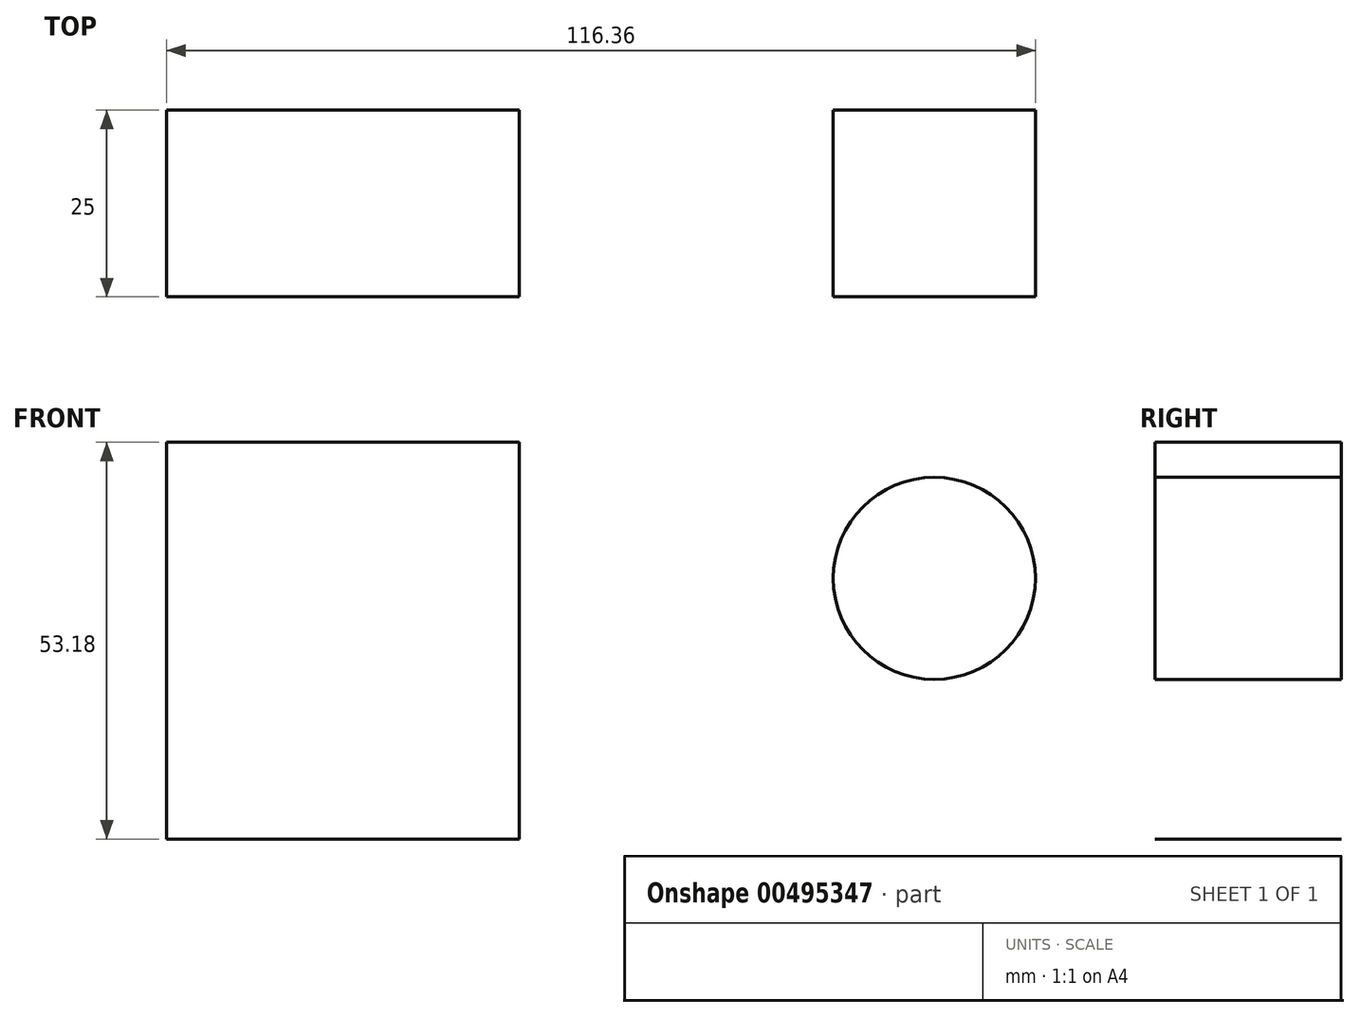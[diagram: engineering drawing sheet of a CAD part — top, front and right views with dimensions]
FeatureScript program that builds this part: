
annotation { "Feature Type Name" : "Feature", "Feature Type Description" : "" }
export const myFeature = defineFeature(function(context is Context, id is Id, definition is map)
    precondition{}
    {
        {
            var Q0;
            Q0=qCreatedBy(makeId("Front.planeOp"),FACE);
            var sketch = newSketch(context, id + "F0", { "sketchPlane" : qUnion([Q0])});
            skLineSegment(sketch, "E0.bottom", {"start": v(-68.86, 20.15) * mm, "end": v(-21.65, 20.15) * mm});
            skLineSegment(sketch, "E0.top", {"start": v(-68.86, -33.03) * mm, "end": v(-21.65, -33.03) * mm});
            skLineSegment(sketch, "E0.left", {"start": v(-68.86, 20.15) * mm, "end": v(-68.86, -33.03) * mm});
            skLineSegment(sketch, "E0.right", {"start": v(-21.65, 20.15) * mm, "end": v(-21.65, -33.03) * mm});
            skCircle(sketch, "E1", {"center": v(33.96, 1.9) * mm, "radius": 13.54 * mm});
            skSolve(sketch);
        }
        {
            var Q0;
            Q0=qSketchRegion(id+"F0",true);
            extrude(context, id + "F1", {"entities" : qUnion([Q0]), "depth" : 25 * mm});
        }
    });
